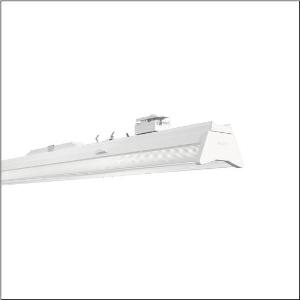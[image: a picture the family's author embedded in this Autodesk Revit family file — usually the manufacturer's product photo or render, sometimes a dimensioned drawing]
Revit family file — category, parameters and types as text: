
# Revit family: licross_r__11_performance_ho_51tm16cn4exm_9d3d
name_source: partatom
category: Lighting Fixtures
units: mm (PartAtom-declared; Revit-internal decimal feet)

## family parameters
Cut with Voids When Loaded = No
Host = Face
Light Source = No
Part Type = Normal
Room Calculation Point = No
Round Connector Dimension = Use Diameter
Shared = No

## types (1)
- --- (1 x LED, 14420 lm, 77.6 W, 4000K)
    Apparent Load = 78 VA
    CIE Flux Codes = 63 87 95 78 100
    Color Rendering = 80
    Color Temperature = 4000K
    Default Elevation = 1800 mm
    Description = Licross® 11 Performance HO, luminaire insert, of sheet steel, galvanised, coil coated, white, length: 1.500mm, width: 120mm, height: 123mm, LED rated luminous flux: 14.420lm, light colour: 840, control gear: ON/OFF Multilumen, CLOi, with plug, 3-pole, with phase selection, mains connection: 220..240V, AC, 50/60Hz, start of lifetime: 78W, end of service life: 87W, halogen-free wiring, primary light control with lens, of plastic, primary optical cover: cover, of PMMA, light emission: direct/indirect distribution, primary light characteristic: symmetric, protection rating (complete): IP40, insulation class (complete): insulation class I (protective earthing), certification: CE, ENEC, VDE, UKCA, protection symbol: D if used in an environment without relevant dust loads with corresponding accessories, impact resistance: IK06, permissible ambient temperature for indoor applications: -35..+35°C, corresponds to IFS (International Featured Standards) requirements for safety and quality in the food industry, reducing of maximum allowable ambient temperature of 5°C with ceiling mounting, LABS conformity tested according to VDMA 24364:2018-05, packaging unit: 1 piece
    Height = 114 mm
    Lamp = 1 x LED
    Lamp Light Flux = 14420 lm
    Lamp Power = 77.6 W
    Lamp count = 1
    Length = 1500 mm
    Luminous efficacy = 186 lm/W
    Manufacturer = Siteco
    ModVariant = No
    Model = 51TM16CN4EXM
    Mounting Place = Ceiling
    Mounting Type = Pendant
    Number of Poles = 1
    OnlyDefault = Yes
    Power Factor = 1
    Product Name = Licross® 11 Performance HO
    Product group = luminaire insert
    ProductGroupID = 901
    Protection Class = Protection class I
    Protection Degree = IP 40
    RLX_Detail_Level = 1
    RLX_Emergency_Light_Flux = 0 lm
    RLX_Emergency_Type = 0
    RLX_Emergency_Type_DB = No
    RlxData = <blob elided: 31893 chars, md5=855fbcdf>
    Socket = socket
    Standby Power = 0 W
    System Light Flux = 14420 lm
    System Power = 78 W
    Type Comments = factory setting: luminous flux: 100 % | (A | C | E) | 181 mA
    Type Image = l_1256138.jpg
    URL = http://relux.com
    VarID = @adj_038355
    Voltage = 0 V
    Weight = 0.00 kg
    Width = 120 mm

## geometry (parser evidence)
native form markers: Blend x4, Sweep x12
no freeform markers — native parametric forms only
